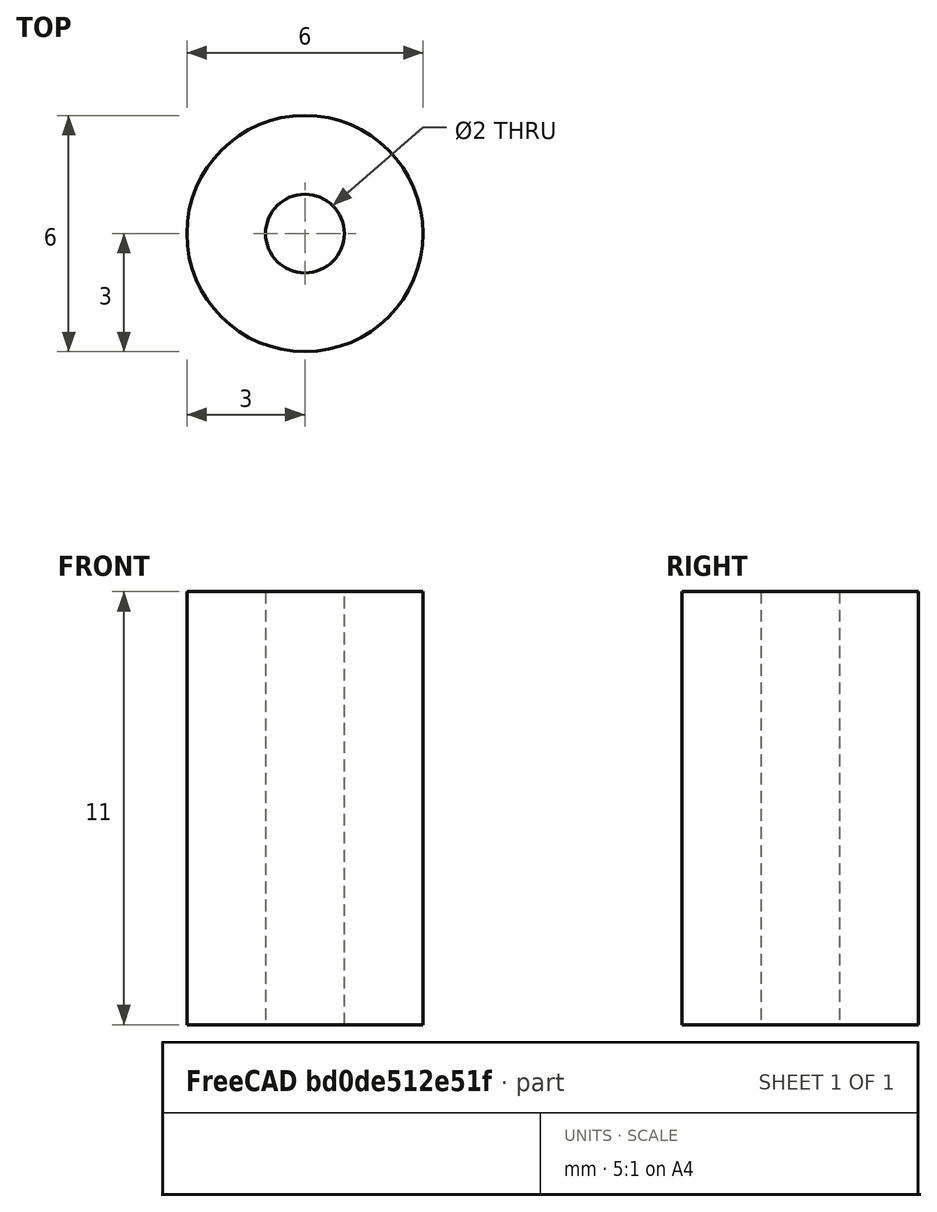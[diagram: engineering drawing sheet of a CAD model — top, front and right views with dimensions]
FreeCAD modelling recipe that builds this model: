
FCSTD DOCUMENT  (FreeCAD 0.19R24415 (Git))
Label: entretoises
License: All rights reserved
LicenseURL: http://en.wikipedia.org/wiki/All_rights_reserved
objects: Spreadsheet::Sheet×1, Sketcher::SketchObject×1, PartDesign::Pad×1, PartDesign::Body×1
note: 4 computed .brp shape members not serialized (recipe doc carries the construction recipe); baked Part::Feature solids carry a one-line shape summary decoded from their .brp

FEATURE [Spreadsheet::Sheet] Spreadsheet
  cells = B2=diametre; C2(dia)=2; B3=hauteur; C3(haut)=11; B4=epaisseur; C4(ep)=4
FEATURE [Sketcher::SketchObject] Sketch
  FullyConstrained = true
  MapMode = 5
  Support = -> [XY_Plane]
  expr: Constraints[3] = Spreadsheet.dia + Spreadsheet.ep
  expr: Constraints[2] = Spreadsheet.dia
  sketch-geometry (2):
    g0: Circle CenterX=0 CenterY=0 CenterZ=0 NormalX=0 NormalY=0 NormalZ=1 AngleXU=0 Radius=1
    g1: Circle CenterX=0 CenterY=0 CenterZ=0 NormalX=0 NormalY=0 NormalZ=1 AngleXU=0 Radius=3
  constraints (4):
    c: Coincident(g0,g-1)
    c: Coincident(g1,g0)
    c: Diameter(g0) = 2
    c: Diameter(g1) = 6
FEATURE [PartDesign::Pad] Pad
  Direction = (1,1,1)
  Length = 11
  Length2 = 100
  Profile = -> Sketch
  Type = 0
  expr: Length = Spreadsheet.haut
FEATURE [PartDesign::Body] Body
  Group = -> [Sketch,Pad]
  Origin = -> Origin
  Tip = -> Pad
